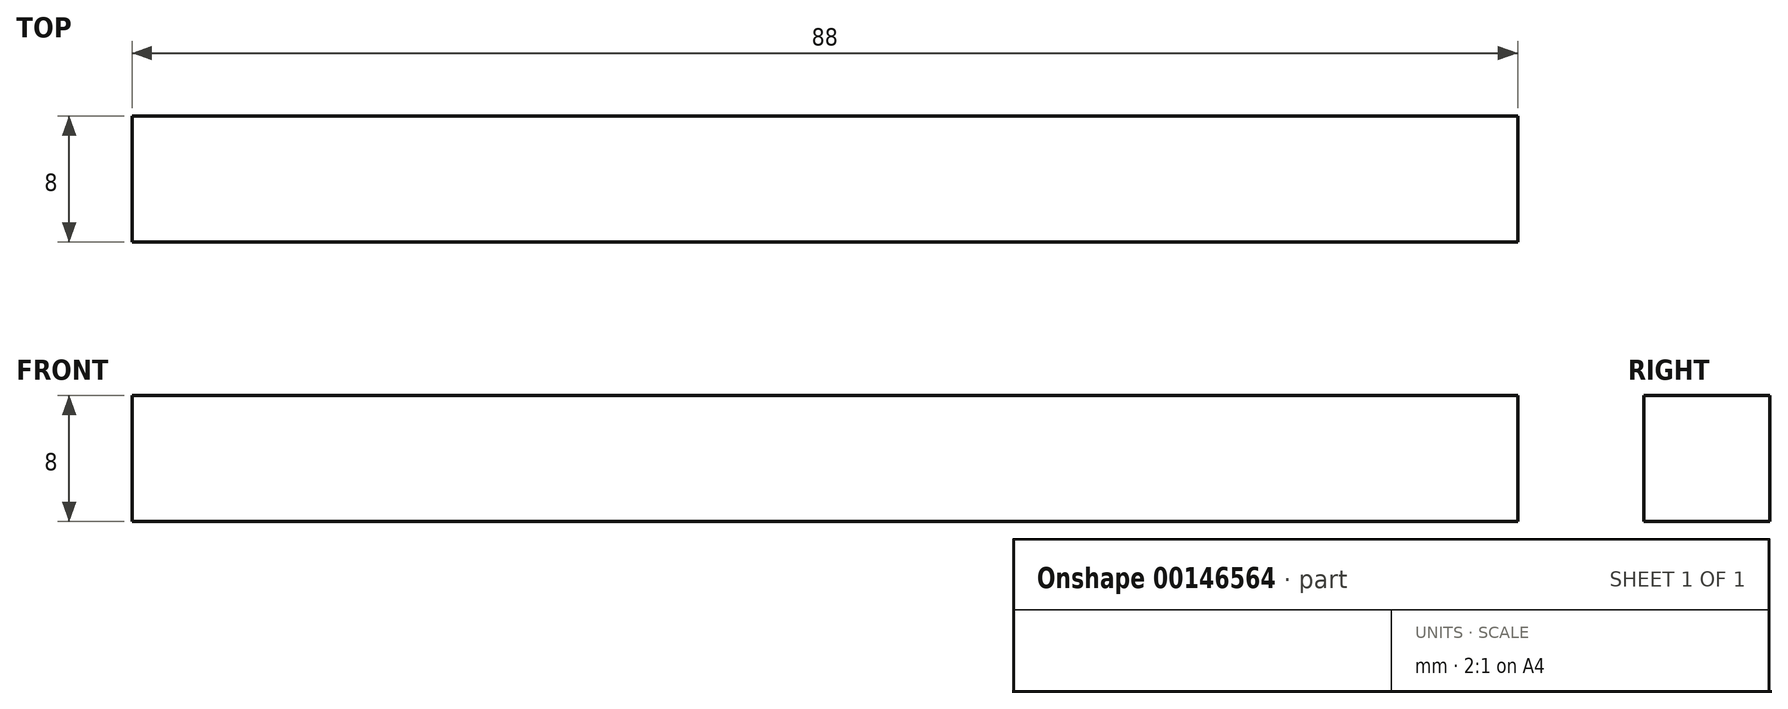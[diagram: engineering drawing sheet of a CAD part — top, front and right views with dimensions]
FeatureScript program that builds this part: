
annotation { "Feature Type Name" : "Feature", "Feature Type Description" : "" }
export const myFeature = defineFeature(function(context is Context, id is Id, definition is map)
    precondition{}
    {
        {
            assignVariable(context, id + "F0", {"name" : "width", "anyValue" : 8});
        }
        {
            var Q0;
            Q0=qCreatedBy(makeId("Front.planeOp"),FACE);
            var sketch = newSketch(context, id + "F1", { "sketchPlane" : qUnion([Q0])});
            skLineSegment(sketch, "E0", {"start": v(-44, 0) * mm, "end": v(-44, 8) * mm});
            skLineSegment(sketch, "E1", {"start": v(-44, 8) * mm, "end": v(44, 8) * mm});
            skLineSegment(sketch, "E2", {"start": v(44, 8) * mm, "end": v(44, 0) * mm});
            skLineSegment(sketch, "E3", {"start": v(44, 0) * mm, "end": v(-44, 0) * mm});
            skSolve(sketch);
        }
        {
            var Q0;
            Q0=makeQuery(id+"F1.imprint","IMPRINT",FACE,{"disambiguationData":[TD([[makeQuery(id+"F1.imprint","IMPRINT",EDGE,{"derivedFrom":sQuery(id+"F1.wireOp",EDGE,"E0")}),-1.0]])]});
            extrude(context, id + "F2", {"entities" : qUnion([Q0]), "depth" : (getVariable(context, 'width')) * mm, "symmetric" : true});
        }
    });
